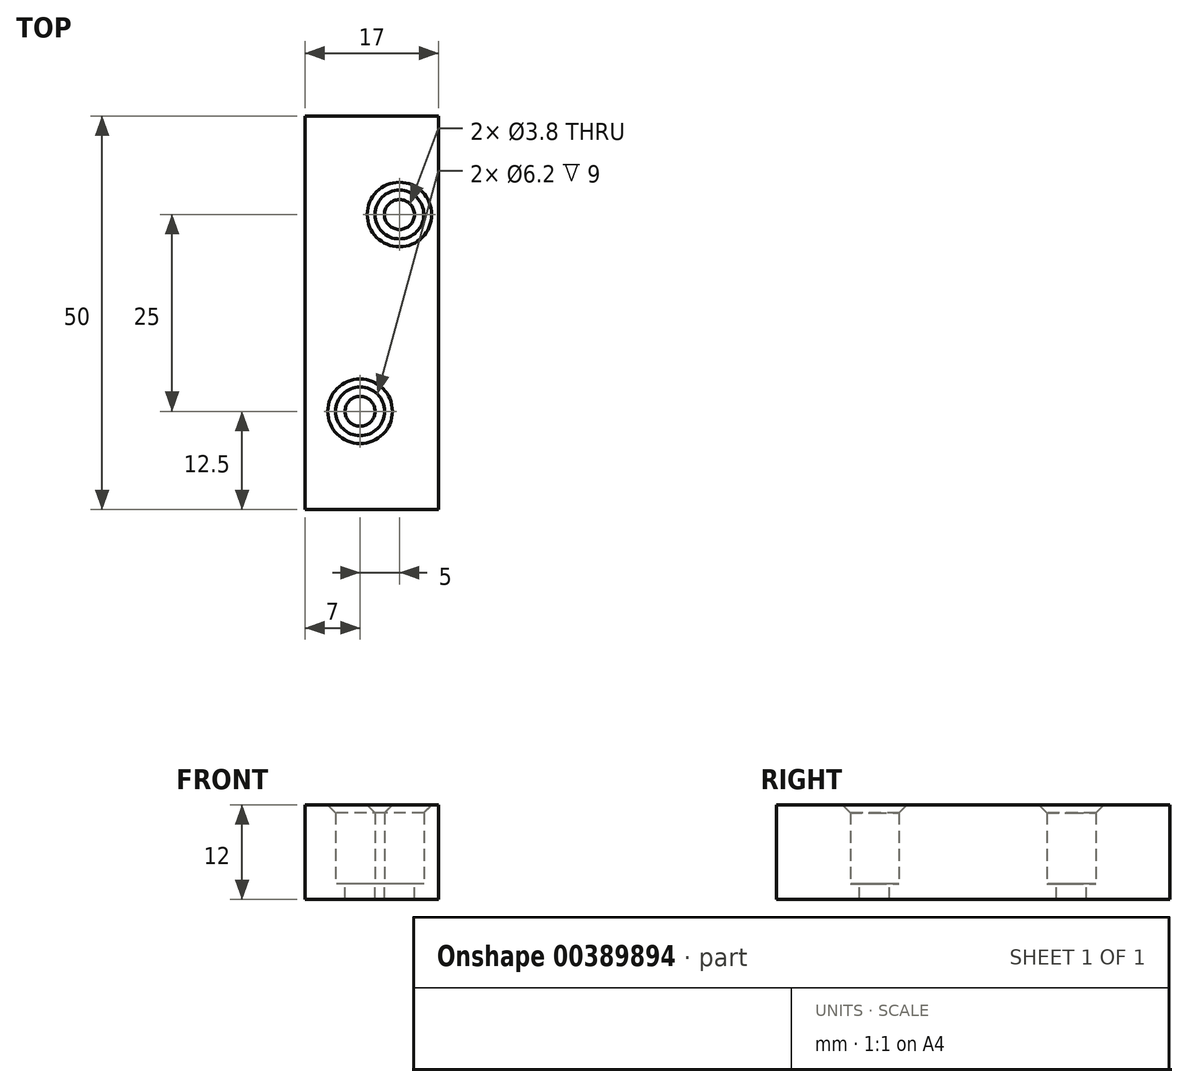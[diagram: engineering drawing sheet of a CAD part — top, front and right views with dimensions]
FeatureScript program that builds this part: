
annotation { "Feature Type Name" : "Feature", "Feature Type Description" : "" }
export const myFeature = defineFeature(function(context is Context, id is Id, definition is map)
    precondition{}
    {
        {
            var Q0;
            Q0=qCreatedBy(makeId("Top.planeOp"),FACE);
            var sketch = newSketch(context, id + "F0", { "sketchPlane" : qUnion([Q0])});
            skLineSegment(sketch, "E0", {"start": v(0, 25) * mm, "end": v(8.5, 25) * mm});
            skLineSegment(sketch, "E1", {"start": v(8.5, 25) * mm, "end": v(8.5, 0) * mm});
            skLineSegment(sketch, "E2.MirrorCS", {"start": v(8.5, -25) * mm, "end": v(8.5, 0) * mm});
            skLineSegment(sketch, "E3.MirrorCS", {"start": v(0, -25) * mm, "end": v(8.5, -25) * mm});
            skLineSegment(sketch, "E4", {"start": v(0, 0) * mm, "end": v(0, 12.5) * mm});
            skLineSegment(sketch, "E5", {"start": v(0, 0) * mm, "end": v(0, -12.5) * mm});
            skLineSegment(sketch, "E6", {"start": v(0, 12.5) * mm, "end": v(3.5, 12.5) * mm});
            skLineSegment(sketch, "E7", {"start": v(0, -12.5) * mm, "end": v(-1.5, -12.5) * mm});
            skLineSegment(sketch, "E8.MirrorCS", {"start": v(0, 25) * mm, "end": v(-8.5, 25) * mm});
            skLineSegment(sketch, "E9.MirrorCS", {"start": v(-8.5, -25) * mm, "end": v(-8.5, 0) * mm});
            skLineSegment(sketch, "E10.MirrorCS", {"start": v(-8.5, 25) * mm, "end": v(-8.5, 0) * mm});
            skLineSegment(sketch, "E11.MirrorCS", {"start": v(0, -25) * mm, "end": v(-8.5, -25) * mm});
            skLineSegment(sketch, "E12.MirrorCS", {"start": v(0, -12.5) * mm, "end": v(1.5, -12.5) * mm});
            skLineSegment(sketch, "E13.MirrorCS", {"start": v(0, 12.5) * mm, "end": v(-3.5, 12.5) * mm});
            skSolve(sketch);
        }
        {
            var Q0;
            Q0=qSketchRegion(id+"F0",true);
            extrude(context, id + "F1", {"entities" : qUnion([Q0]), "depth" : 10 * mm, "hasSecondDirection" : true, "secondDirectionOppositeDirection" : true, "secondDirectionDepth" : 2 * mm});
        }
        {
            var Q0;
            Q0=qCreatedBy(makeId("Top.planeOp"),FACE);
            var sketch = newSketch(context, id + "F2", { "sketchPlane" : qUnion([Q0])});
            skCircle(sketch, "E14", {"center": v(3.5, 12.5) * mm, "radius": 3.1 * mm});
            skLineSegment(sketch, "E15", {"start": v(0, -119.55) * mm, "end": v(0, 110.32) * mm, "construction": true});
            skLineSegment(sketch, "E16", {"start": v(-127.65, 0) * mm, "end": v(113.38, 0) * mm, "construction": true});
            skCircle(sketch, "E17", {"center": v(-1.5, -12.5) * mm, "radius": 3.1 * mm});
            skSolve(sketch);
        }
        {
            var Q0;
            Q0=qCreatedBy(makeId("Top.planeOp"),FACE);
            var sketch = newSketch(context, id + "F3", { "sketchPlane" : qUnion([Q0])});
            skCircle(sketch, "E18", {"center": v(3.5, 12.5) * mm, "radius": 1.9 * mm});
            skCircle(sketch, "E19", {"center": v(-1.5, -12.5) * mm, "radius": 1.9 * mm});
            skSolve(sketch);
        }
        {
            var Q0;
            Q0 = qSketchRegion(id + "F3", true);
            extrude(context, id + "F4", {"entities" : qUnion([Q0]), "operationType" : NewBodyOperationType.REMOVE, "oppositeDirection" : true, "depth" : 25 * mm});
        }
        {
            var Q0;
            Q0 = qSketchRegion(id + "F2", true);
            extrude(context, id + "F5", {"entities" : qUnion([Q0]), "operationType" : NewBodyOperationType.REMOVE, "depth" : 25 * mm});
        }
        {
            var Q0;
            Q0=makeQuery(id+"F5.boolean.opBoolean","INTERSECT",EDGE,{"derivedFrom":[makeQuery(id+"F1.opExtrude","CAP_FACE",FACE,{"disambiguationData":[OSD([sQuery(id+"F0.wireOp",EDGE,"df51decc-40ad-429f-aa7a-2f92934fcf6c2.MirrorCS"),sQuery(id+"F0.wireOp",EDGE,"df51decc-40ad-429f-aa7a-2f92934fcf6c4.MirrorCS"),sQuery(id+"F0.wireOp",EDGE,"E1"),sQuery(id+"F0.wireOp",EDGE,"E0"),sQuery(id+"F0.wireOp",EDGE,"E2.MirrorCS"),sQuery(id+"F0.wireOp",EDGE,"E3.MirrorCS"),sQuery(id+"F0.wireOp",EDGE,"7c23db01-5317-4992-90b2-9f42a5ef55ce12.MirrorCS"),sQuery(id+"F0.wireOp",EDGE,"7c23db01-5317-4992-90b2-9f42a5ef55ce13.MirrorCS")])],"isStart":false}),makeQuery(id+"F5.opExtrude","SWEPT_FACE",FACE,{"disambiguationData":[OSD([sQuery(id+"F2.wireOp",EDGE,"E17")])]})]});
            var Q1;
            Q1=makeQuery(id+"F5.boolean.opBoolean","INTERSECT",EDGE,{"derivedFrom":[makeQuery(id+"F1.opExtrude","CAP_FACE",FACE,{"disambiguationData":[OSD([sQuery(id+"F0.wireOp",EDGE,"df51decc-40ad-429f-aa7a-2f92934fcf6c2.MirrorCS"),sQuery(id+"F0.wireOp",EDGE,"df51decc-40ad-429f-aa7a-2f92934fcf6c4.MirrorCS"),sQuery(id+"F0.wireOp",EDGE,"E1"),sQuery(id+"F0.wireOp",EDGE,"E0"),sQuery(id+"F0.wireOp",EDGE,"E2.MirrorCS"),sQuery(id+"F0.wireOp",EDGE,"E3.MirrorCS"),sQuery(id+"F0.wireOp",EDGE,"7c23db01-5317-4992-90b2-9f42a5ef55ce12.MirrorCS"),sQuery(id+"F0.wireOp",EDGE,"7c23db01-5317-4992-90b2-9f42a5ef55ce13.MirrorCS")])],"isStart":false}),makeQuery(id+"F5.opExtrude","SWEPT_FACE",FACE,{"disambiguationData":[OSD([sQuery(id+"F2.wireOp",EDGE,"E14")])]})]});
            chamfer(context, id + "F6", {"entities" : qUnion([Q0, Q1]), "width" : 1 * mm, "tangentPropagation" : true});
        }
    });
